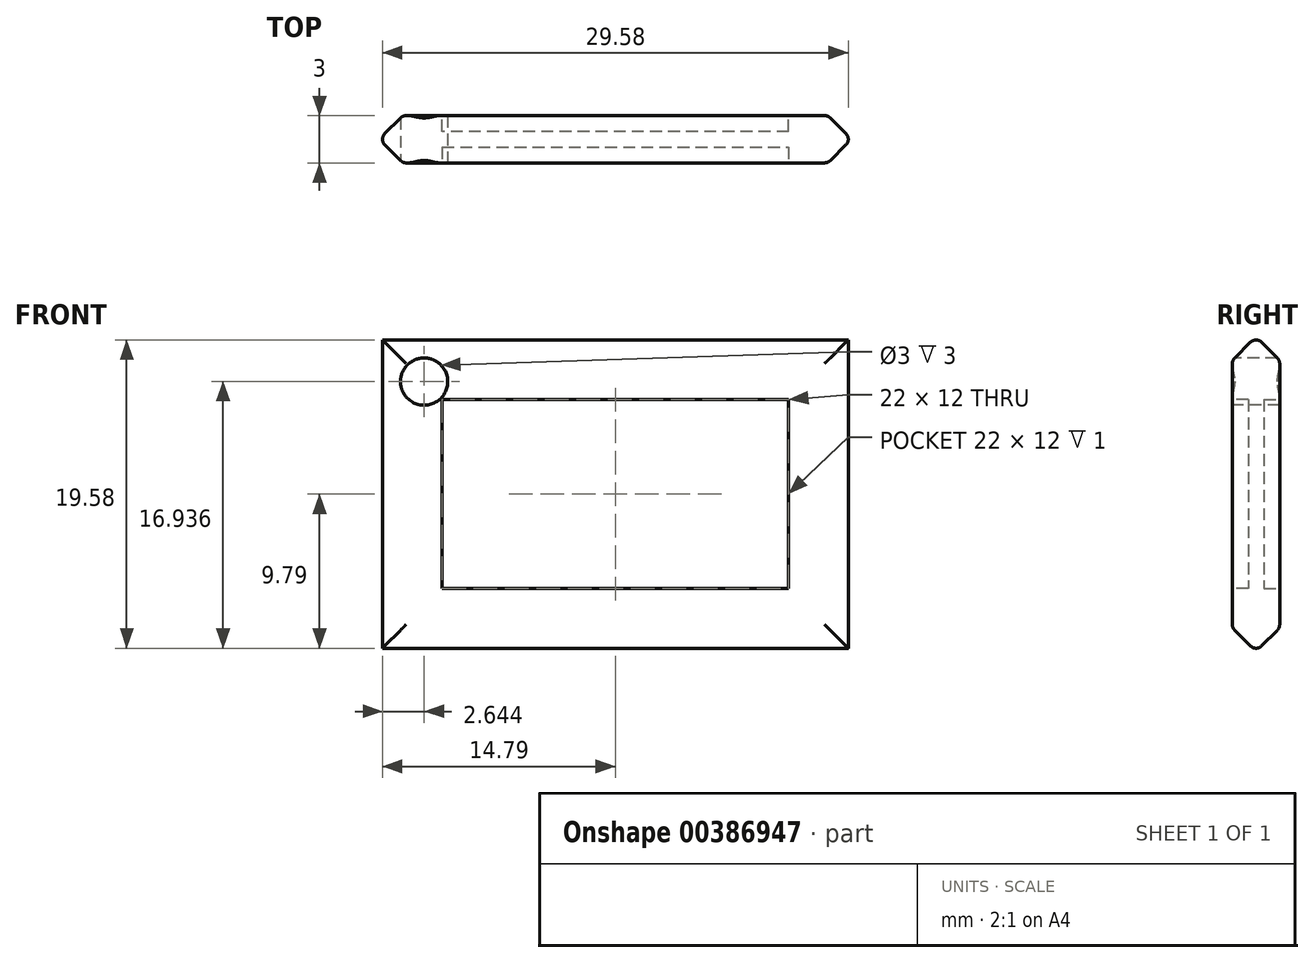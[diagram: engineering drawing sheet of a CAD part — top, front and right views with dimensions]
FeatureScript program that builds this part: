
annotation { "Feature Type Name" : "Feature", "Feature Type Description" : "" }
export const myFeature = defineFeature(function(context is Context, id is Id, definition is map)
    precondition{}
    {
        {
            var Q0;
            Q0=qCreatedBy(makeId("Front.planeOp"),FACE);
            var sketch = newSketch(context, id + "F0", { "sketchPlane" : qUnion([Q0])});
            skLineSegment(sketch, "E0.bottom", {"start": v(-15, 10) * mm, "end": v(15, 10) * mm});
            skLineSegment(sketch, "E0.top", {"start": v(-15, -10) * mm, "end": v(15, -10) * mm});
            skLineSegment(sketch, "E0.left", {"start": v(-15, 10) * mm, "end": v(-15, -10) * mm});
            skLineSegment(sketch, "E0.right", {"start": v(15, 10) * mm, "end": v(15, -10) * mm});
            skSolve(sketch);
        }
        {
            var Q0;
            Q0 = qSketchRegion(id + "F0", true);
            extrude(context, id + "F1", {"entities" : qUnion([Q0]), "depth" : 3 * mm});
        }
        {
            var Q0;
            Q0=makeQuery(id+"F1.opExtrude","CAP_FACE",FACE,{"disambiguationData":[OSD([sQuery(id+"F0.wireOp",EDGE,"E0.bottom"),sQuery(id+"F0.wireOp",EDGE,"E0.top"),sQuery(id+"F0.wireOp",EDGE,"E0.left"),sQuery(id+"F0.wireOp",EDGE,"E0.right")])],"isStart":false});
            var Q1;
            Q1=makeQuery(id+"F1.opExtrude","CAP_FACE",FACE,{"disambiguationData":[OSD([sQuery(id+"F0.wireOp",EDGE,"E0.bottom"),sQuery(id+"F0.wireOp",EDGE,"E0.top"),sQuery(id+"F0.wireOp",EDGE,"E0.left"),sQuery(id+"F0.wireOp",EDGE,"E0.right")])],"isStart":true});
            chamfer(context, id + "F2", {"entities" : qUnion([Q0, Q1]), "width" : 1.5 * mm, "tangentPropagation" : true});
        }
        {
            var Q0;
            Q0=makeQuery(id+"F1.opExtrude","CAP_FACE",FACE,{"disambiguationData":[OSD([sQuery(id+"F0.wireOp",EDGE,"E0.bottom"),sQuery(id+"F0.wireOp",EDGE,"E0.top"),sQuery(id+"F0.wireOp",EDGE,"E0.left"),sQuery(id+"F0.wireOp",EDGE,"E0.right")])],"isStart":true});
            var sketch = newSketch(context, id + "F3", { "sketchPlane" : qUnion([Q0])});
            skLineSegment(sketch, "E1.bottom", {"start": v(-11, 6) * mm, "end": v(11, 6) * mm});
            skLineSegment(sketch, "E1.top", {"start": v(-11, -6) * mm, "end": v(11, -6) * mm});
            skLineSegment(sketch, "E1.left", {"start": v(-11, 6) * mm, "end": v(-11, -6) * mm});
            skLineSegment(sketch, "E1.right", {"start": v(11, 6) * mm, "end": v(11, -6) * mm});
            skSolve(sketch);
        }
        {
            var Q0;
            Q0 = qSketchRegion(id + "F3", true);
            extrude(context, id + "F4", {"entities" : qUnion([Q0]), "operationType" : NewBodyOperationType.REMOVE, "oppositeDirection" : true, "depth" : 1 * mm});
        }
        {
            var Q0;
            Q0=makeQuery(id+"F1.opExtrude","CAP_FACE",FACE,{"disambiguationData":[OSD([sQuery(id+"F0.wireOp",EDGE,"E0.bottom"),sQuery(id+"F0.wireOp",EDGE,"E0.top"),sQuery(id+"F0.wireOp",EDGE,"E0.left"),sQuery(id+"F0.wireOp",EDGE,"E0.right")])],"isStart":false});
            var sketch = newSketch(context, id + "F5", { "sketchPlane" : qUnion([Q0])});
            skLineSegment(sketch, "E2.bottom", {"start": v(-11, 6) * mm, "end": v(11, 6) * mm});
            skLineSegment(sketch, "E2.top", {"start": v(-11, -6) * mm, "end": v(11, -6) * mm});
            skLineSegment(sketch, "E2.left", {"start": v(-11, 6) * mm, "end": v(-11, -6) * mm});
            skLineSegment(sketch, "E2.right", {"start": v(11, 6) * mm, "end": v(11, -6) * mm});
            skSolve(sketch);
        }
        {
            var Q0;
            Q0 = qSketchRegion(id + "F5", true);
            extrude(context, id + "F6", {"entities" : qUnion([Q0]), "operationType" : NewBodyOperationType.REMOVE, "oppositeDirection" : true, "depth" : 1 * mm});
        }
        {
            var Q0;
            {var subQ0=sQuery(id+"F0.wireOp",EDGE,"E0.top");Q0=makeQuery(id+"F2.opChamfer","BLEND_EDGE",EDGE,{"blendedFrom":[makeQuery(id+"F1.opExtrude","CAP_EDGE",EDGE,{"disambiguationData":[OSD([subQ0])],"isStart":true}),makeQuery(id+"F1.opExtrude","CAP_EDGE",EDGE,{"disambiguationData":[OSD([subQ0])],"isStart":false})],"blendedInto":[]});}
            var Q1;
            {var subQ0=sQuery(id+"F0.wireOp",EDGE,"E0.left");Q1=makeQuery(id+"F2.opChamfer","BLEND_EDGE",EDGE,{"blendedFrom":[makeQuery(id+"F1.opExtrude","CAP_EDGE",EDGE,{"disambiguationData":[OSD([subQ0])],"isStart":true}),makeQuery(id+"F1.opExtrude","CAP_EDGE",EDGE,{"disambiguationData":[OSD([subQ0])],"isStart":false})],"blendedInto":[]});}
            var Q2;
            {var subQ0=sQuery(id+"F0.wireOp",EDGE,"E0.bottom");Q2=makeQuery(id+"F2.opChamfer","BLEND_EDGE",EDGE,{"blendedFrom":[makeQuery(id+"F1.opExtrude","CAP_EDGE",EDGE,{"disambiguationData":[OSD([subQ0])],"isStart":true}),makeQuery(id+"F1.opExtrude","CAP_EDGE",EDGE,{"disambiguationData":[OSD([subQ0])],"isStart":false})],"blendedInto":[]});}
            var Q3;
            {var subQ0=sQuery(id+"F0.wireOp",EDGE,"E0.right");Q3=makeQuery(id+"F2.opChamfer","BLEND_EDGE",EDGE,{"blendedFrom":[makeQuery(id+"F1.opExtrude","CAP_EDGE",EDGE,{"disambiguationData":[OSD([subQ0])],"isStart":true}),makeQuery(id+"F1.opExtrude","CAP_EDGE",EDGE,{"disambiguationData":[OSD([subQ0])],"isStart":false})],"blendedInto":[]});}
            fillet(context, id + "F7", {"entities" : qUnion([Q0, Q1, Q2, Q3]), "radius" : 0.5 * mm, "tangentPropagation" : true, "allowEdgeOverflow" : false});
        }
        {
            var Q0;
            {var subQ0=sQuery(id+"F0.wireOp",EDGE,"E0.right");Q0=makeQuery(id+"F2.opChamfer","BLEND_EDGE",EDGE,{"blendedFrom":[makeQuery(id+"F1.opExtrude","CAP_EDGE",EDGE,{"disambiguationData":[OSD([subQ0])],"isStart":true}),makeQuery(id+"F1.opExtrude","CAP_FACE",FACE,{"disambiguationData":[OSD([sQuery(id+"F0.wireOp",EDGE,"E0.bottom"),sQuery(id+"F0.wireOp",EDGE,"E0.top"),sQuery(id+"F0.wireOp",EDGE,"E0.left"),subQ0])],"isStart":true})],"blendedInto":[makeQuery(id+"F1.opExtrude","CAP_FACE",FACE,{"disambiguationData":[OSD([sQuery(id+"F0.wireOp",EDGE,"E0.bottom"),sQuery(id+"F0.wireOp",EDGE,"E0.top"),sQuery(id+"F0.wireOp",EDGE,"E0.left"),subQ0])],"isStart":true})]});}
            var Q1;
            {var subQ0=sQuery(id+"F0.wireOp",EDGE,"E0.bottom");Q1=makeQuery(id+"F2.opChamfer","BLEND_EDGE",EDGE,{"blendedFrom":[makeQuery(id+"F1.opExtrude","CAP_EDGE",EDGE,{"disambiguationData":[OSD([subQ0])],"isStart":true}),makeQuery(id+"F1.opExtrude","CAP_FACE",FACE,{"disambiguationData":[OSD([subQ0,sQuery(id+"F0.wireOp",EDGE,"E0.top"),sQuery(id+"F0.wireOp",EDGE,"E0.left"),sQuery(id+"F0.wireOp",EDGE,"E0.right")])],"isStart":true})],"blendedInto":[makeQuery(id+"F1.opExtrude","CAP_FACE",FACE,{"disambiguationData":[OSD([subQ0,sQuery(id+"F0.wireOp",EDGE,"E0.top"),sQuery(id+"F0.wireOp",EDGE,"E0.left"),sQuery(id+"F0.wireOp",EDGE,"E0.right")])],"isStart":true})]});}
            var Q2;
            {var subQ0=sQuery(id+"F0.wireOp",EDGE,"E0.top");Q2=makeQuery(id+"F2.opChamfer","BLEND_EDGE",EDGE,{"blendedFrom":[makeQuery(id+"F1.opExtrude","CAP_EDGE",EDGE,{"disambiguationData":[OSD([subQ0])],"isStart":true}),makeQuery(id+"F1.opExtrude","CAP_FACE",FACE,{"disambiguationData":[OSD([sQuery(id+"F0.wireOp",EDGE,"E0.bottom"),subQ0,sQuery(id+"F0.wireOp",EDGE,"E0.left"),sQuery(id+"F0.wireOp",EDGE,"E0.right")])],"isStart":true})],"blendedInto":[makeQuery(id+"F1.opExtrude","CAP_FACE",FACE,{"disambiguationData":[OSD([sQuery(id+"F0.wireOp",EDGE,"E0.bottom"),subQ0,sQuery(id+"F0.wireOp",EDGE,"E0.left"),sQuery(id+"F0.wireOp",EDGE,"E0.right")])],"isStart":true})]});}
            var Q3;
            {var subQ0=sQuery(id+"F0.wireOp",EDGE,"E0.left");Q3=makeQuery(id+"F2.opChamfer","BLEND_EDGE",EDGE,{"blendedFrom":[makeQuery(id+"F1.opExtrude","CAP_EDGE",EDGE,{"disambiguationData":[OSD([subQ0])],"isStart":true}),makeQuery(id+"F1.opExtrude","CAP_FACE",FACE,{"disambiguationData":[OSD([sQuery(id+"F0.wireOp",EDGE,"E0.bottom"),sQuery(id+"F0.wireOp",EDGE,"E0.top"),subQ0,sQuery(id+"F0.wireOp",EDGE,"E0.right")])],"isStart":true})],"blendedInto":[makeQuery(id+"F1.opExtrude","CAP_FACE",FACE,{"disambiguationData":[OSD([sQuery(id+"F0.wireOp",EDGE,"E0.bottom"),sQuery(id+"F0.wireOp",EDGE,"E0.top"),subQ0,sQuery(id+"F0.wireOp",EDGE,"E0.right")])],"isStart":true})]});}
            fillet(context, id + "F8", {"entities" : qUnion([Q0, Q1, Q2, Q3]), "radius" : 0.5 * mm, "tangentPropagation" : true, "allowEdgeOverflow" : false});
        }
        {
            var Q0;
            {var subQ0=sQuery(id+"F0.wireOp",EDGE,"E0.left");Q0=makeQuery(id+"F2.opChamfer","BLEND_EDGE",EDGE,{"blendedFrom":[makeQuery(id+"F1.opExtrude","CAP_EDGE",EDGE,{"disambiguationData":[OSD([subQ0])],"isStart":false}),makeQuery(id+"F1.opExtrude","CAP_FACE",FACE,{"disambiguationData":[OSD([sQuery(id+"F0.wireOp",EDGE,"E0.bottom"),sQuery(id+"F0.wireOp",EDGE,"E0.top"),subQ0,sQuery(id+"F0.wireOp",EDGE,"E0.right")])],"isStart":false})],"blendedInto":[makeQuery(id+"F1.opExtrude","CAP_FACE",FACE,{"disambiguationData":[OSD([sQuery(id+"F0.wireOp",EDGE,"E0.bottom"),sQuery(id+"F0.wireOp",EDGE,"E0.top"),subQ0,sQuery(id+"F0.wireOp",EDGE,"E0.right")])],"isStart":false})]});}
            var Q1;
            {var subQ0=sQuery(id+"F0.wireOp",EDGE,"E0.top");Q1=makeQuery(id+"F2.opChamfer","BLEND_EDGE",EDGE,{"blendedFrom":[makeQuery(id+"F1.opExtrude","CAP_EDGE",EDGE,{"disambiguationData":[OSD([subQ0])],"isStart":false}),makeQuery(id+"F1.opExtrude","CAP_FACE",FACE,{"disambiguationData":[OSD([sQuery(id+"F0.wireOp",EDGE,"E0.bottom"),subQ0,sQuery(id+"F0.wireOp",EDGE,"E0.left"),sQuery(id+"F0.wireOp",EDGE,"E0.right")])],"isStart":false})],"blendedInto":[makeQuery(id+"F1.opExtrude","CAP_FACE",FACE,{"disambiguationData":[OSD([sQuery(id+"F0.wireOp",EDGE,"E0.bottom"),subQ0,sQuery(id+"F0.wireOp",EDGE,"E0.left"),sQuery(id+"F0.wireOp",EDGE,"E0.right")])],"isStart":false})]});}
            var Q2;
            {var subQ0=sQuery(id+"F0.wireOp",EDGE,"E0.bottom");Q2=makeQuery(id+"F2.opChamfer","BLEND_EDGE",EDGE,{"blendedFrom":[makeQuery(id+"F1.opExtrude","CAP_EDGE",EDGE,{"disambiguationData":[OSD([subQ0])],"isStart":false}),makeQuery(id+"F1.opExtrude","CAP_FACE",FACE,{"disambiguationData":[OSD([subQ0,sQuery(id+"F0.wireOp",EDGE,"E0.top"),sQuery(id+"F0.wireOp",EDGE,"E0.left"),sQuery(id+"F0.wireOp",EDGE,"E0.right")])],"isStart":false})],"blendedInto":[makeQuery(id+"F1.opExtrude","CAP_FACE",FACE,{"disambiguationData":[OSD([subQ0,sQuery(id+"F0.wireOp",EDGE,"E0.top"),sQuery(id+"F0.wireOp",EDGE,"E0.left"),sQuery(id+"F0.wireOp",EDGE,"E0.right")])],"isStart":false})]});}
            var Q3;
            {var subQ0=sQuery(id+"F0.wireOp",EDGE,"E0.right");Q3=makeQuery(id+"F2.opChamfer","BLEND_EDGE",EDGE,{"blendedFrom":[makeQuery(id+"F1.opExtrude","CAP_EDGE",EDGE,{"disambiguationData":[OSD([subQ0])],"isStart":false}),makeQuery(id+"F1.opExtrude","CAP_FACE",FACE,{"disambiguationData":[OSD([sQuery(id+"F0.wireOp",EDGE,"E0.bottom"),sQuery(id+"F0.wireOp",EDGE,"E0.top"),sQuery(id+"F0.wireOp",EDGE,"E0.left"),subQ0])],"isStart":false})],"blendedInto":[makeQuery(id+"F1.opExtrude","CAP_FACE",FACE,{"disambiguationData":[OSD([sQuery(id+"F0.wireOp",EDGE,"E0.bottom"),sQuery(id+"F0.wireOp",EDGE,"E0.top"),sQuery(id+"F0.wireOp",EDGE,"E0.left"),subQ0])],"isStart":false})]});}
            fillet(context, id + "F9", {"entities" : qUnion([Q0, Q1, Q2, Q3]), "radius" : 0.5 * mm, "tangentPropagation" : true, "allowEdgeOverflow" : false});
        }
        {
            var Q0;
            Q0=makeQuery(id+"F1.opExtrude","CAP_FACE",FACE,{"disambiguationData":[OSD([sQuery(id+"F0.wireOp",EDGE,"E0.bottom"),sQuery(id+"F0.wireOp",EDGE,"E0.top"),sQuery(id+"F0.wireOp",EDGE,"E0.left"),sQuery(id+"F0.wireOp",EDGE,"E0.right")])],"isStart":false});
            var sketch = newSketch(context, id + "F10", { "sketchPlane" : qUnion([Q0])});
            skCircle(sketch, "E3", {"center": v(-12.15, 7.15) * mm, "radius": 1.5 * mm});
            skSolve(sketch);
        }
        {
            var Q0;
            Q0 = qSketchRegion(id + "F10", true);
            extrude(context, id + "F11", {"entities" : qUnion([Q0]), "operationType" : NewBodyOperationType.REMOVE, "oppositeDirection" : true, "depth" : 25 * mm});
        }
    });
